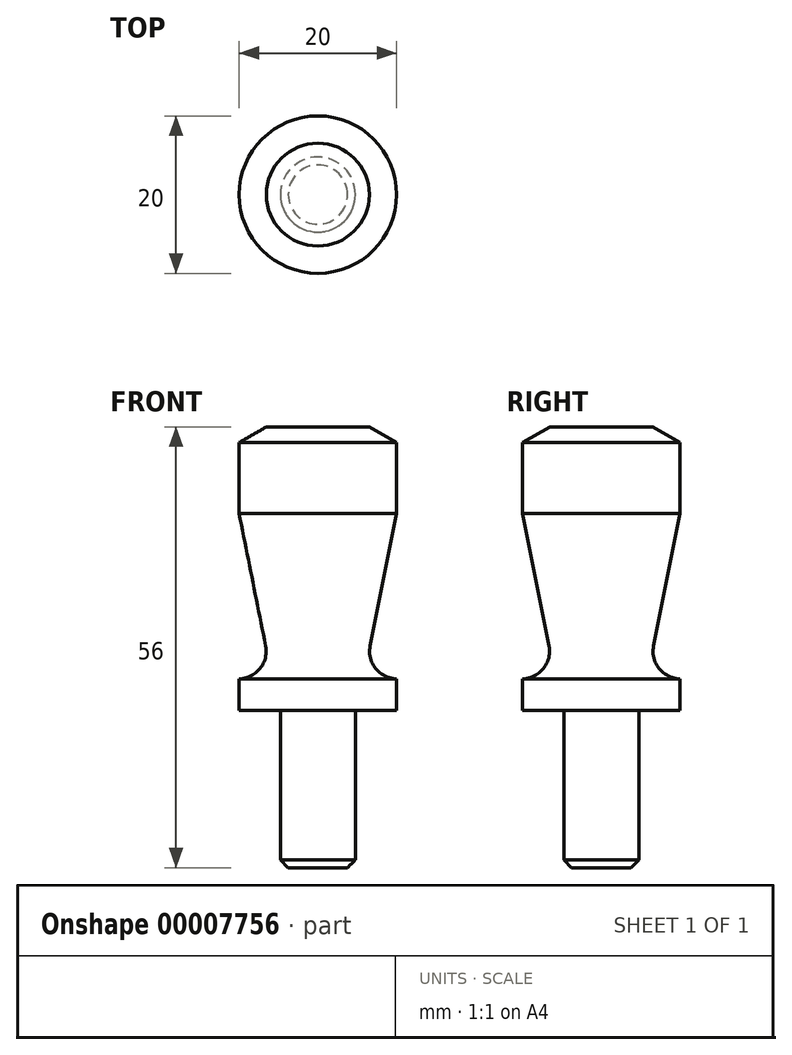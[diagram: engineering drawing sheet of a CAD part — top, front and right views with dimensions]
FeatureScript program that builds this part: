
annotation { "Feature Type Name" : "Feature", "Feature Type Description" : "" }
export const myFeature = defineFeature(function(context is Context, id is Id, definition is map)
    precondition{}
    {
        {
            var Q0;
            Q0=qCreatedBy(makeId("Front.planeOp"),FACE);
            var sketch = newSketch(context, id + "F0", { "sketchPlane" : qUnion([Q0])});
            skLineSegment(sketch, "E0", {"start": v(0, 16) * mm, "end": v(10, 16) * mm});
            skLineSegment(sketch, "E1", {"start": v(10, 16) * mm, "end": v(10, 5) * mm});
            skLineSegment(sketch, "E2", {"start": v(9.77, -16) * mm, "end": v(10, -16.02) * mm});
            skLineSegment(sketch, "E3", {"start": v(10, -16.02) * mm, "end": v(10, -20) * mm});
            skLineSegment(sketch, "E4", {"start": v(10, -20) * mm, "end": v(4.76, -20) * mm});
            skLineSegment(sketch, "E5", {"start": v(4.76, -20) * mm, "end": v(4.76, -40) * mm});
            skLineSegment(sketch, "E6", {"start": v(4.76, -40) * mm, "end": v(0, -40) * mm});
            skLineSegment(sketch, "E7", {"start": v(0, -40) * mm, "end": v(0, 16) * mm});
            skPoint(sketch, "E8.visualSharp", {"position": v(6.5, -15.72) * mm});
            skArc(sketch, "E8.filletArc", {"start": v(6.64, -11.83) * mm, "mid": v(7.27, -14.62) * mm, "end": v(9.77, -16) * mm});
            skLineSegment(sketch, "E9", {"start": v(6.64, -11.83) * mm, "end": v(10, 5) * mm});
            skSolve(sketch);
        }
        {
            var Q0;
            Q0 = qSketchRegion(id + "F0", true);
            var Q1;
            Q1=sQuery(id+"F0.wireOp",EDGE,"E7");
            revolve(context, id + "F1", {"entities" : qUnion([Q0]), "axis" : qUnion([Q1]), "revolveType" : RevolveType.FULL});
        }
        {
            var Q0;
            Q0=makeQuery(id+"F1.opRevolve","SWEPT_EDGE",EDGE,{"disambiguationData":[OSD([sQuery(id+"F0.wireOp",EDGE,"E0"),sQuery(id+"F0.wireOp",EDGE,"E1")])]});
            chamfer(context, id + "F2", {"entities" : qUnion([Q0]), "chamferType" : ChamferType.OFFSET_ANGLE, "width" : 2 * mm, "oppositeDirection" : false, "angle" : 60 * degree, "tangentPropagation" : true});
        }
        {
            var Q0;
            Q0=makeQuery(id+"F1.opRevolve","SWEPT_EDGE",EDGE,{"disambiguationData":[OSD([sQuery(id+"F0.wireOp",EDGE,"E5"),sQuery(id+"F0.wireOp",EDGE,"E6")])]});
            chamfer(context, id + "F3", {"entities" : qUnion([Q0]), "width" : 1 * mm, "tangentPropagation" : true});
        }
    });
